# Revit family: Nivellierbare Kassette für Tubus, RKFR, 20-25, 7
name_source: partatom
category: Generic Models
revit_build: Autodesk Revit 2015 (Build: 20140606_1530(x64)
units: mm (PartAtom-declared; Revit-internal decimal feet)

## types (2) — shared parameters
Diameter = 274 mm  [stored 0.89895 ft]
Diameter 1 = 266 mm
Height = 150 mm
Height 1 = 37 mm
HeightCalc = 150 mm
Manufacturer = OBO Bettermann
URL = http://www.obo-bettermann.com

## per-type parameters (varying)
| type | Cut depth | GTIN | Manufacturer Art.No. | Material |
| RKFR2 7 V20 | 20 mm  [stored 0.0656168 ft] | 4012195869504 | 7409426 | Stainless Steel, Polished |
| RKFR2 7 V25 | 25 mm  [stored 0.082021 ft] | 4012195869511 | 7409428 | Stainless Steel |

note: column(s) folded — value = type name in every type: Article Type

note: [stored X ft] marks values corroborated as IEEE doubles in the binary element streams (Revit-internal decimal feet)

## geometry (parser evidence)
native form markers: Sweep x2
no freeform markers — native parametric forms only
